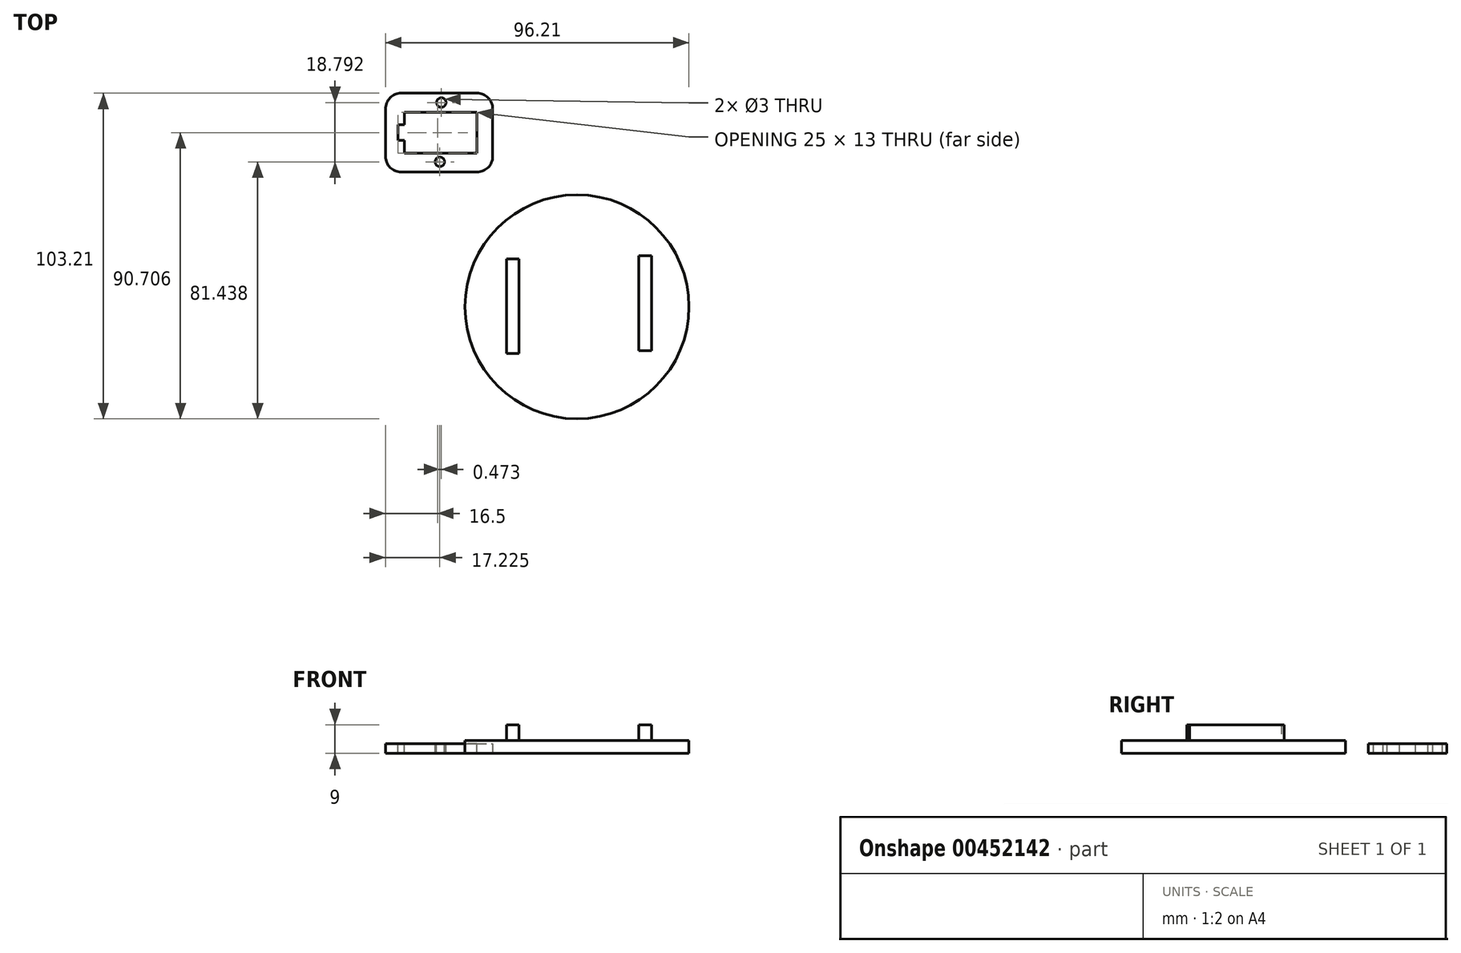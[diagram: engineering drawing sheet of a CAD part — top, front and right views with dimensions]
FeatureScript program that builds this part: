
annotation { "Feature Type Name" : "Feature", "Feature Type Description" : "" }
export const myFeature = defineFeature(function(context is Context, id is Id, definition is map)
    precondition{}
    {
        {
            var Q0;
            Q0=qCreatedBy(makeId("Top.planeOp"),FACE);
            var sketch = newSketch(context, id + "F0", { "sketchPlane" : qUnion([Q0])});
            skLineSegment(sketch, "E0.bottom", {"start": v(-34, 22.03) * mm, "end": v(0, 22.03) * mm});
            skLineSegment(sketch, "E0.top", {"start": v(-34, 47.03) * mm, "end": v(0, 47.03) * mm});
            skLineSegment(sketch, "E0.left", {"start": v(-34, 22.03) * mm, "end": v(-34, 47.03) * mm});
            skLineSegment(sketch, "E0.right", {"start": v(0, 22.03) * mm, "end": v(0, 47.03) * mm});
            skSolve(sketch);
        }
        {
            var Q0;
            Q0=makeQuery(id+"F0.imprint","IMPRINT",FACE,{"disambiguationData":[TD([[makeQuery(id+"F0.imprint","IMPRINT",EDGE,{"derivedFrom":sQuery(id+"F0.wireOp",EDGE,"E0.bottom")}),1.0]])]});
            extrude(context, id + "F1", {"entities" : qUnion([Q0]), "depth" : 3 * mm});
        }
        {
            var Q0;
            Q0=makeQuery(id+"F1.opExtrude","SWEPT_EDGE",EDGE,{"disambiguationData":[OSD([sQuery(id+"F0.wireOp",EDGE,"E0.top"),sQuery(id+"F0.wireOp",EDGE,"E0.right")])]});
            var Q1;
            Q1=makeQuery(id+"F1.opExtrude","SWEPT_EDGE",EDGE,{"disambiguationData":[OSD([sQuery(id+"F0.wireOp",EDGE,"E0.bottom"),sQuery(id+"F0.wireOp",EDGE,"E0.right")])]});
            var Q2;
            Q2=makeQuery(id+"F1.opExtrude","SWEPT_EDGE",EDGE,{"disambiguationData":[OSD([sQuery(id+"F0.wireOp",EDGE,"E0.bottom"),sQuery(id+"F0.wireOp",EDGE,"E0.left")])]});
            var Q3;
            Q3=makeQuery(id+"F1.opExtrude","SWEPT_EDGE",EDGE,{"disambiguationData":[OSD([sQuery(id+"F0.wireOp",EDGE,"E0.top"),sQuery(id+"F0.wireOp",EDGE,"E0.left")])]});
            fillet(context, id + "F2", {"entities" : qUnion([Q0, Q1, Q2, Q3]), "radius" : 5 * mm, "tangentPropagation" : true, "allowEdgeOverflow" : false});
        }
        {
            var Q0;
            Q0=makeQuery(id+"F1.opExtrude","CAP_FACE",FACE,{"disambiguationData":[OSD([sQuery(id+"F0.wireOp",EDGE,"E0.bottom"),sQuery(id+"F0.wireOp",EDGE,"E0.top"),sQuery(id+"F0.wireOp",EDGE,"E0.left"),sQuery(id+"F0.wireOp",EDGE,"E0.right")])],"isStart":false});
            var sketch = newSketch(context, id + "F3", { "sketchPlane" : qUnion([Q0])});
            skLineSegment(sketch, "E1", {"start": v(-5, 22.03) * mm, "end": v(-5, 28.03) * mm});
            skLineSegment(sketch, "E2", {"start": v(-5, 47.03) * mm, "end": v(-5, 41.03) * mm});
            skLineSegment(sketch, "E3.bottom", {"start": v(-5, 28.03) * mm, "end": v(-28, 28.03) * mm});
            skLineSegment(sketch, "E3.top", {"start": v(-5, 41.03) * mm, "end": v(-28, 41.03) * mm});
            skLineSegment(sketch, "E3.left", {"start": v(-5, 28.03) * mm, "end": v(-5, 41.03) * mm});
            skLineSegment(sketch, "E3.right", {"start": v(-28, 28.03) * mm, "end": v(-28, 41.03) * mm});
            skLineSegment(sketch, "E4", {"start": v(-28, 28.03) * mm, "end": v(-28, 32.03) * mm});
            skLineSegment(sketch, "E5.bottom", {"start": v(-28, 32.03) * mm, "end": v(-30, 32.03) * mm});
            skLineSegment(sketch, "E5.top", {"start": v(-28, 37.03) * mm, "end": v(-30, 37.03) * mm});
            skLineSegment(sketch, "E5.left", {"start": v(-28, 32.03) * mm, "end": v(-28, 37.03) * mm});
            skLineSegment(sketch, "E5.right", {"start": v(-30, 32.03) * mm, "end": v(-30, 37.03) * mm});
            skLineSegment(sketch, "E6", {"start": v(-28, 41.03) * mm, "end": v(-16.5, 41.03) * mm});
            skCircle(sketch, "E7", {"center": v(-16.3, 44.05) * mm, "radius": 1.5 * mm});
            skLineSegment(sketch, "E8", {"start": v(-28, 28.03) * mm, "end": v(-16.5, 28.03) * mm});
            skCircle(sketch, "E9", {"center": v(-16.78, 25.26) * mm, "radius": 1.5 * mm});
            skSolve(sketch);
        }
        {
            var Q0;
            Q0 = qSketchRegion(id + "F3", true);
            extrude(context, id + "F4", {"entities" : qUnion([Q0]), "operationType" : NewBodyOperationType.REMOVE, "oppositeDirection" : true, "depth" : 25 * mm});
        }
        {
            var Q0;
            Q0=qCreatedBy(makeId("Top.planeOp"),FACE);
            var sketch = newSketch(context, id + "F5", { "sketchPlane" : qUnion([Q0])});
            skCircle(sketch, "E10", {"center": v(26.7, -20.68) * mm, "radius": 35.5 * mm});
            skSolve(sketch);
        }
        {
            var Q0;
            Q0 = qSketchRegion(id + "F5", true);
            extrude(context, id + "F6", {"entities" : qUnion([Q0]), "depth" : 4 * mm});
        }
        {
            var Q0;
            Q0=makeQuery(id+"F6.opExtrude","CAP_FACE",FACE,{"disambiguationData":[OSD([sQuery(id+"F5.wireOp",EDGE,"E10")])],"isStart":false});
            var sketch = newSketch(context, id + "F7", { "sketchPlane" : qUnion([Q0])});
            skLineSegment(sketch, "E11", {"start": v(56.3, -1.08) * mm, "end": v(46.3, -1.08) * mm});
            skLineSegment(sketch, "E12", {"start": v(46.3, -1.08) * mm, "end": v(46.3, 8.92) * mm});
            skLineSegment(sketch, "E13.bottom", {"start": v(50.32, -4.56) * mm, "end": v(46.32, -4.56) * mm});
            skLineSegment(sketch, "E13.top", {"start": v(50.32, -34.56) * mm, "end": v(46.32, -34.56) * mm});
            skLineSegment(sketch, "E13.left", {"start": v(50.32, -4.56) * mm, "end": v(50.32, -34.56) * mm});
            skLineSegment(sketch, "E13.right", {"start": v(46.32, -4.56) * mm, "end": v(46.32, -34.56) * mm});
            skLineSegment(sketch, "E14", {"start": v(-8.78, -19.69) * mm, "end": v(2.27, -19.69) * mm});
            skLineSegment(sketch, "E15.bottom", {"start": v(4.35, -5.48) * mm, "end": v(8.35, -5.48) * mm});
            skLineSegment(sketch, "E15.top", {"start": v(4.35, -35.48) * mm, "end": v(8.35, -35.48) * mm});
            skLineSegment(sketch, "E15.left", {"start": v(4.35, -5.48) * mm, "end": v(4.35, -35.48) * mm});
            skLineSegment(sketch, "E15.right", {"start": v(8.35, -5.48) * mm, "end": v(8.35, -35.48) * mm});
            skSolve(sketch);
        }
        {
            var Q0;
            Q0 = qSketchRegion(id + "F7", true);
            extrude(context, id + "F8", {"entities" : qUnion([Q0]), "operationType" : NewBodyOperationType.ADD, "depth" : 5 * mm});
        }
    });
